# Revit family: 1900H Coat Cupboard
name_source: partatom
category: Casework
revit_build: Autodesk Revit 2016 (Build: 20150220_1215(x64)
units: mm (PartAtom-declared; Revit-internal decimal feet)

## family parameters
Always vertical = Yes
Cut with Voids When Loaded = No
OmniClass Number = 23.40.35.00
OmniClass Title = Casework
Room Calculation Point = No
Shared = No
Work Plane-Based = No

## types (3) — shared parameters
AB Lock = No
AssetType = Fixed
Carcass Material = MFC
Depth = 600 mm
DurationUnit = Years
E4 Lock = No
Finish = Matt
Height = 1900 mm  [stored 6.2336 ft]
M3 Lock = No
ManufactureName = Bisley
Manufacturer = Bisley
ManufacturerURL = www.bisley.com
Material = MFC
Model = Lockerwall
NBSDescription = General fittings, furnishings and equipment system
NBSReference = 45-35-80/380
Name = 1900H Coat Cupboard
NominalHeight = 1900 mm  [stored 6.2336 ft]
NominalLength = 600 mm
SustainabilityPerformance = FSC Approved
URL = www.bisley.com
Uniclass2015Code = Pr_40_30_78_48
Uniclass2015Title = Lockers
Uniclass2015Version = 3.1
WarrantyDescription = 5 Years Parts & Labour
WarrantyDurationLabour = 5
WarrantyDurationParts = 5
WarrantyDurationUnit = Years
WarrantyGuarantorLabour = www.bisley.com
WarrantyGuarantorParts = www.bisley.com

## per-type parameters (varying)
| type | 1 Door | 2 Door | NominalWidth | T Handle 1 Door | T Handle 2 Door | Width |
| LW0519CC | Yes | No | 500 mm  [stored 1.64042 ft] | Yes | No | 500 mm  [stored 1.64042 ft] |
| LW0819CC | No | Yes | 800 mm  [stored 2.62467 ft] | No | Yes | 800 mm  [stored 2.62467 ft] |
| LW1019CC | No | Yes | 1000 mm  [stored 3.28084 ft] | No | Yes | 1000 mm  [stored 3.28084 ft] |

note: column(s) folded — value = type name in every type: ModelReference

note: [stored X ft] marks values corroborated as IEEE doubles in the binary element streams (Revit-internal decimal feet)

## geometry (parser evidence)
native form markers: Sweep x15
no freeform markers — native parametric forms only
